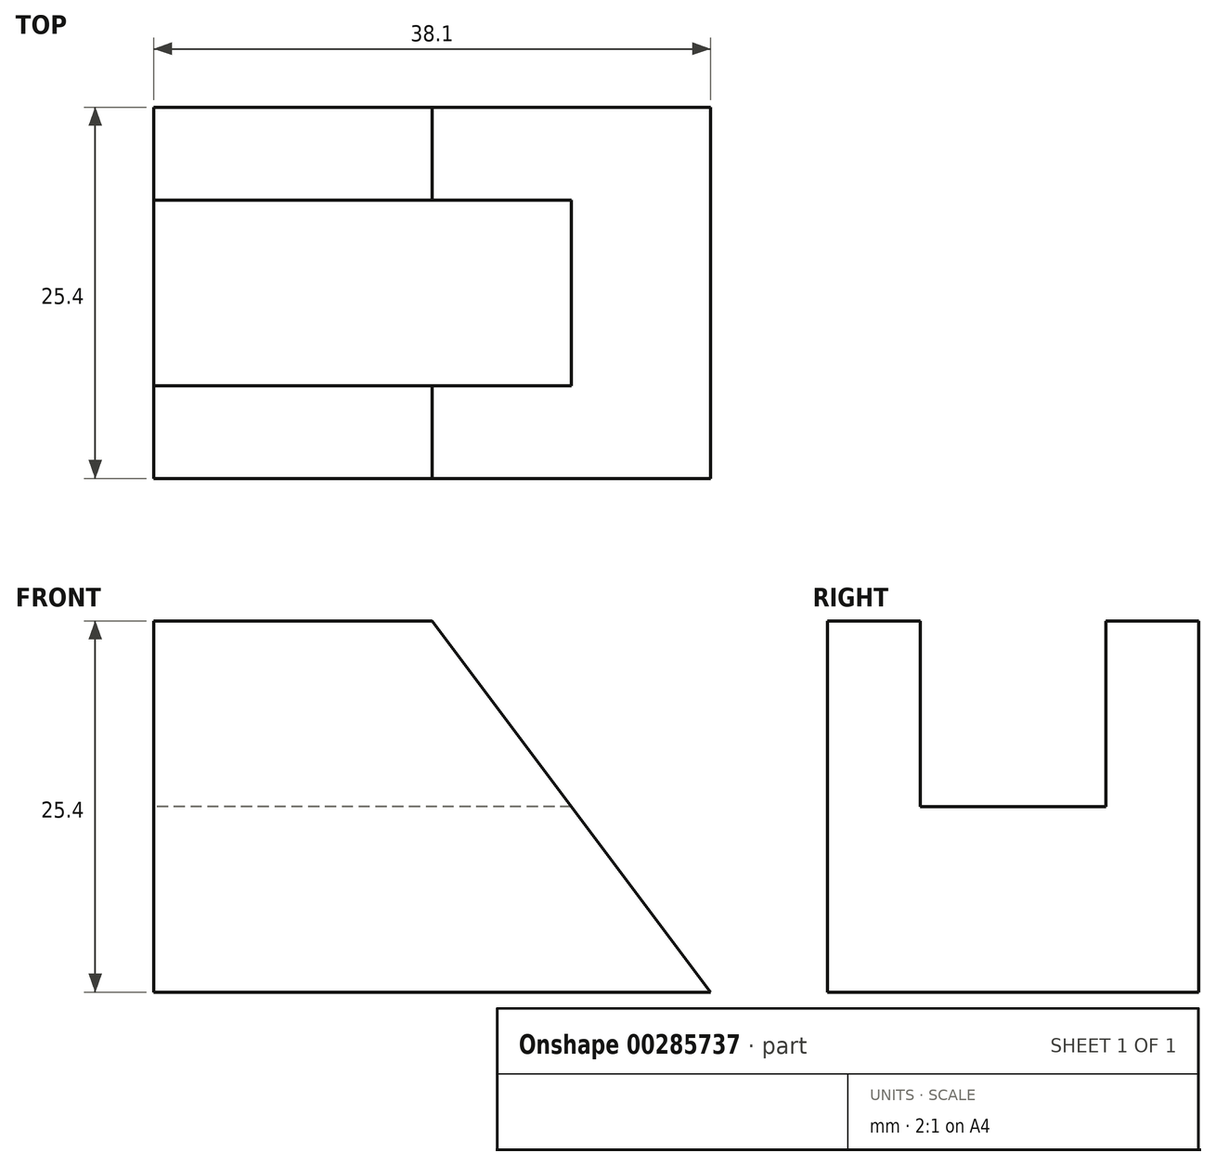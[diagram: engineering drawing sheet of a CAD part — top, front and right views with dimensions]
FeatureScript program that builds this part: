
annotation { "Feature Type Name" : "Feature", "Feature Type Description" : "" }
export const myFeature = defineFeature(function(context is Context, id is Id, definition is map)
    precondition{}
    {
        {
            var Q0;
            Q0=qCreatedBy(makeId("Front.planeOp"),FACE);
            var sketch = newSketch(context, id + "F0", { "sketchPlane" : qUnion([Q0])});
            skLineSegment(sketch, "E0", {"start": v(0, 0) * mm, "end": v(0, 25.4) * mm});
            skLineSegment(sketch, "E1", {"start": v(0, 25.4) * mm, "end": v(19.05, 25.4) * mm});
            skLineSegment(sketch, "E2", {"start": v(19.05, 25.4) * mm, "end": v(38.1, 0) * mm});
            skLineSegment(sketch, "E3", {"start": v(38.1, 0) * mm, "end": v(0, 0) * mm});
            skSolve(sketch);
        }
        {
            var Q0;
            Q0 = qSketchRegion(id + "F0", true);
            extrude(context, id + "F1", {"entities" : qUnion([Q0]), "endBound" : BoundingType.SYMMETRIC, "depth" : 25.4 * mm});
        }
        {
            var Q0;
            Q0=qCreatedBy(makeId("Right.planeOp"),FACE);
            var sketch = newSketch(context, id + "F2", { "sketchPlane" : qUnion([Q0])});
            skLineSegment(sketch, "E4", {"start": v(-6.35, 25.4) * mm, "end": v(-6.35, 12.7) * mm});
            skLineSegment(sketch, "E5", {"start": v(-6.35, 12.7) * mm, "end": v(6.35, 12.7) * mm});
            skLineSegment(sketch, "E6", {"start": v(6.35, 12.7) * mm, "end": v(6.35, 25.4) * mm});
            skLineSegment(sketch, "E7", {"start": v(6.35, 25.4) * mm, "end": v(-6.35, 25.4) * mm});
            skSolve(sketch);
        }
        {
            var Q0;
            Q0 = qSketchRegion(id + "F2", true);
            extrude(context, id + "F3", {"entities" : qUnion([Q0]), "operationType" : NewBodyOperationType.REMOVE, "endBound" : BoundingType.THROUGH_ALL, "depth" : 25.4 * mm});
        }
    });
